# Revit family: LeL Tago 1.3
name_source: partatom
category: Lighting Fixtures
units: mm (PartAtom-declared; Revit-internal decimal feet)

## family parameters
Cut with Voids When Loaded = Yes
Host = Face
Light Source = No
Part Type = Normal
Room Calculation Point = No
Round Connector Dimension = Use Diameter
Shared = No

## types (7) — shared parameters
Accessories = WCTG13A0T outer casing
Alimentazione = 230 V
Apparent Load = 51 VA
CCT = 3000 K
CRI = 80
Default Elevation = 1219 mm
Description = Outdoor Linear Profile
Finish = LeL Black
IK = IK09
IP = IP65 IP67 IP69
Lamp = LED
Lenght = 1020 mm  [stored 3.34646 ft]
Manufacturer = L&L Luce&Light
Model = TG13
Outercasing = 1060 mm
Rated Power supply = 230 V
URL = https://www.lucelight.it
Wattage = 51 W
Weight = 4.08 kg

## per-type parameters (varying)
| type | Optic |
| 1.3 A 51W | TAGO Light source : 1.3 A 51W |
| 1.3 G 51W | TAGO Light source : 1.3 G 51W |
| 1.3 K 69° 51W | TAGO Light source : 1.3 K 69° 51W |
| 1.3 L 29° 51W | TAGO Light source : 1.3 L 29° 51W |
| 1.3 M 17° 51W | TAGO Light source : 1.3 M 17° 51W |
| 1.3 S 11° 51W | TAGO Light source : 1.3 S 11° 51W |
| 1.3 W 20°x49° 51W | TAGO Light source : 1.3 W 20°x49° 51W |

note: [stored X ft] marks values corroborated as IEEE doubles in the binary element streams (Revit-internal decimal feet)

## geometry (parser evidence)
native form markers: Sweep x3
no freeform markers — native parametric forms only
